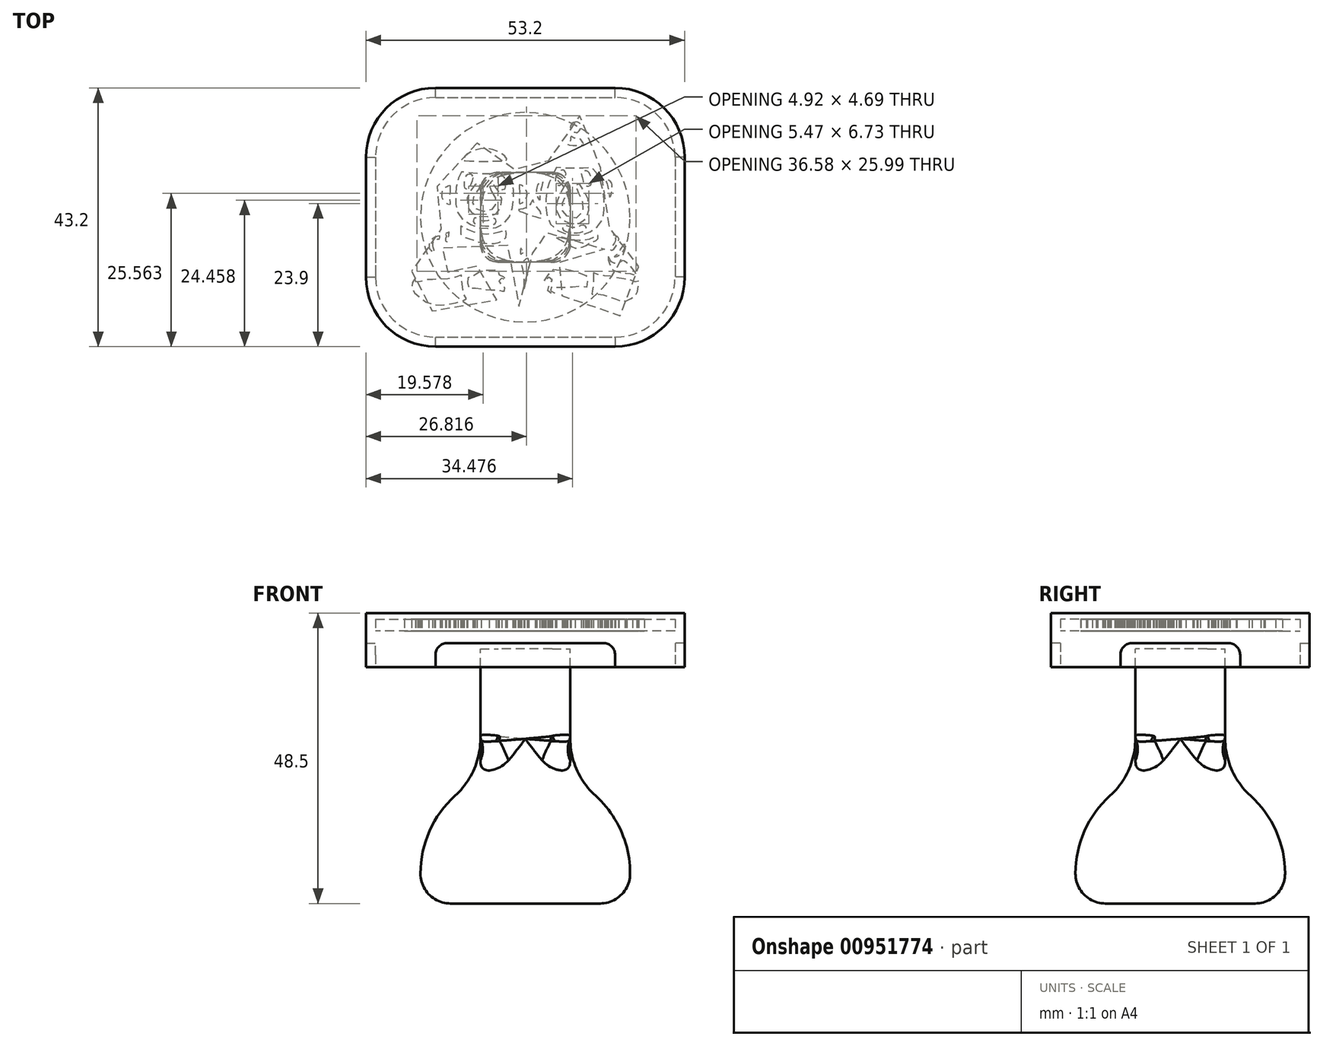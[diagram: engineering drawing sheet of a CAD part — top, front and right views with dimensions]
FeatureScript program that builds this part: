
annotation { "Feature Type Name" : "Feature", "Feature Type Description" : "" }
export const myFeature = defineFeature(function(context is Context, id is Id, definition is map)
    precondition{}
    {
        {
            var Q0;
            Q0=qCreatedBy(makeId("Top.planeOp"),FACE);
            var sketch = newSketch(context, id + "F0", { "sketchPlane" : qUnion([Q0])});
            skLineSegment(sketch, "E0.bottom", {"start": v(-25, 20) * mm, "end": v(25, 20) * mm});
            skLineSegment(sketch, "E0.top", {"start": v(-25, -20) * mm, "end": v(25, -20) * mm});
            skLineSegment(sketch, "E0.left", {"start": v(-25, 20) * mm, "end": v(-25, -20) * mm});
            skLineSegment(sketch, "E0.right", {"start": v(25, 20) * mm, "end": v(25, -20) * mm});
            skPoint(sketch, "E0.middle", {"position": v(0, 0) * mm});
            skSolve(sketch);
        }
        {
            var Q0;
            Q0 = qSketchRegion(id + "F0", true);
            extrude(context, id + "F1", {"entities" : qUnion([Q0]), "oppositeDirection" : true, "depth" : 6 * mm, "offsetDistance" : 25 * mm});
        }
        {
            var Q0;
            Q0=qCreatedBy(makeId("Top.planeOp"),FACE);
            var sketch = newSketch(context, id + "F2", { "sketchPlane" : qUnion([Q0])});
            skPoint(sketch, "E1", {"position": v(0, 16.86) * mm});
            skPoint(sketch, "E2", {"position": v(-20, 0) * mm});
            skFitSpline(sketch, "E3", {"points": [v(-8.08, 12.38) * mm, v(-8.81, 12.12) * mm, v(-9.62, 11.72) * mm, v(-10.36, 11.3) * mm, v(-10.9, 10.85) * mm, v(-11.21, 10.47) * mm, v(-11.41, 10.09) * mm, v(-11.6, 9.5) * mm, v(-11.77, 9.03) * mm, v(-11.88, 8.77) * mm, v(-11.9, 8.4) * mm, v(-11.68, 8) * mm, v(-11.76, 7.76) * mm, v(-12.03, 7.27) * mm, v(-12.19, 6.87) * mm, v(-12.34, 6.5) * mm, v(-12.45, 6.4) * mm, v(-13, 6.27) * mm, v(-13.92, 5.82) * mm, v(-14.38, 5.5) * mm, v(-14.78, 5.09) * mm, v(-15, 4.59) * mm, v(-15.05, 3.88) * mm, v(-15, 3.2) * mm, v(-14.79, 2.65) * mm, v(-14.5, 2.2) * mm, v(-13.81, 1.54) * mm, v(-13.23, 1.23) * mm, v(-12.68, 1.04) * mm, v(-12.39, 0.99) * mm, v(-12.33, 0.87) * mm, v(-12.15, 0.43) * mm, v(-11.89, -0.13) * mm, v(-11.63, -0.6) * mm, v(-11.62, -0.67) * mm, v(-11.71, -0.82) * mm, v(-12.06, -1.11) * mm, v(-12.37, -1.28) * mm, v(-12.95, -1.46) * mm, v(-13.26, -1.54) * mm, v(-13.5, -1.64) * mm, v(-14.05, -1.97) * mm, v(-14.23, -2.05) * mm, v(-14.45, -2.13) * mm, v(-14.88, -2.27) * mm, v(-15.54, -2.46) * mm, v(-16.07, -2.73) * mm, v(-16.64, -3.29) * mm, v(-16.85, -3.46) * mm, v(-17.23, -3.67) * mm, v(-17.63, -3.95) * mm, v(-17.82, -4.33) * mm, v(-17.95, -4.95) * mm, v(-17.92, -5.48) * mm, v(-17.84, -5.77) * mm, v(-17.84, -6.08) * mm, v(-17.88, -6.58) * mm, v(-17.8, -6.98) * mm, v(-17.65, -7.21) * mm, v(-17.63, -7.39) * mm, v(-17.78, -7.58) * mm, v(-18.2, -8.05) * mm, v(-18.56, -8.45) * mm, v(-18.98, -9.02) * mm, v(-19.57, -10) * mm, v(-19.88, -10.58) * mm, v(-20.17, -11.52) * mm, v(-20.16, -11.87) * mm, v(-19.7, -12.89) * mm, v(-19.23, -13.4) * mm, v(-18.28, -14.22) * mm, v(-17.78, -14.62) * mm, v(-17.3, -15.03) * mm, v(-17.25, -15.17) * mm, v(-17.34, -15.62) * mm, v(-17.34, -16.45) * mm, v(-17.23, -16.58) * mm, v(-16.53, -16.56) * mm, v(-16.4, -16.31) * mm, v(-16.3, -15.7) * mm, v(-16.24, -15.48) * mm, v(-16.1, -15.48) * mm, v(-15.79, -15.6) * mm, v(-14.78, -15.7) * mm, v(-13.86, -15.66) * mm, v(-12.92, -15.6) * mm, v(-11.74, -15.32) * mm, v(-10.78, -15.06) * mm, v(-9.64, -14.74) * mm, v(-8.83, -14.36) * mm, v(-8.48, -13.83) * mm, v(-8.4, -13.39) * mm, v(-8.38, -12.92) * mm, v(-8.3, -12.84) * mm, v(-7.52, -12.97) * mm, v(-6.65, -13.05) * mm, v(-6.12, -13.13) * mm, v(-5.83, -13.23) * mm, v(-5.71, -13.43) * mm, v(-5.36, -13.7) * mm, v(-4.81, -13.8) * mm, v(-3.92, -13.75) * mm, v(-2.96, -13.33) * mm, v(-2.56, -12.87) * mm, v(-2.31, -12.03) * mm, v(-2.15, -11.25) * mm, v(-2.12, -10.26) * mm, v(-2.34, -9.74) * mm, v(-2.6, -9.3) * mm, v(-2.9, -8.69) * mm, v(-3.33, -8.19) * mm, v(-3.98, -7.9) * mm, v(-4.6, -7.83) * mm, v(-5.42, -7.88) * mm, v(-6.2, -7.93) * mm, v(-6.94, -7.85) * mm, v(-7.5, -7.95) * mm, v(-8.18, -8.22) * mm, v(-8.73, -8.56) * mm, v(-9.1, -8.85) * mm, v(-9.27, -8.91) * mm, v(-9.53, -8.72) * mm, v(-9.98, -8.51) * mm, v(-10.56, -8.53) * mm, v(-11.24, -8.75) * mm, v(-11.61, -8.87) * mm, v(-11.5, -8.64) * mm, v(-11.36, -8.07) * mm, v(-11.23, -6.94) * mm, v(-11.3, -6.28) * mm, v(-11.6, -5.94) * mm, v(-11.9, -5.9) * mm, v(-12.14, -6.13) * mm, v(-12.26, -6.87) * mm, v(-12.35, -7.71) * mm, v(-12.59, -8.57) * mm, v(-12.82, -9.03) * mm, v(-12.96, -9.24) * mm, v(-13.83, -9.37) * mm, v(-14.94, -9.4) * mm, v(-15.96, -9.32) * mm, v(-17.1, -9.26) * mm, v(-17.68, -9.17) * mm, v(-17.64, -9.02) * mm, v(-17.3, -8.6) * mm, v(-16.63, -7.98) * mm, v(-16.22, -7.73) * mm, v(-16, -7.66) * mm, v(-15.7, -7.4) * mm, v(-15.4, -7.15) * mm, v(-15.02, -6.97) * mm, v(-14.62, -6.86) * mm, v(-14.32, -6.63) * mm, v(-14.14, -6.26) * mm, v(-14.1, -5.92) * mm, v(-14.13, -5.53) * mm, v(-14.04, -5.34) * mm, v(-13.77, -5.08) * mm, v(-13.51, -5) * mm, v(-13.1, -5.05) * mm, v(-12.67, -5.08) * mm, v(-12.36, -4.97) * mm, v(-12.08, -4.63) * mm, v(-11.97, -4.36) * mm, v(-11.85, -4.1) * mm, v(-11.51, -3.99) * mm, v(-11.16, -4.07) * mm, v(-10.2, -4.38) * mm, v(-9.16, -4.72) * mm, v(-8.27, -5.04) * mm, v(-7.47, -5.25) * mm, v(-6.7, -5.4) * mm, v(-5.86, -5.43) * mm, v(-5.09, -5.42) * mm, v(-4.26, -5.25) * mm, v(-3.4, -4.93) * mm, v(-2.8, -4.5) * mm, v(-2.38, -4.08) * mm, v(-2.2, -3.73) * mm, v(-2.1, -3.54) * mm, v(-2.04, -3.7) * mm, v(-1.94, -4.34) * mm, v(-1.89, -5.08) * mm, v(-1.8, -6.13) * mm, v(-1.75, -7.04) * mm, v(-1.64, -7.96) * mm, v(-1.55, -8.7) * mm, v(-1.37, -9.62) * mm, v(-1.28, -10.32) * mm, v(-1.26, -11.23) * mm, v(-1.18, -12.5) * mm, v(-1.14, -13.54) * mm, v(-1.07, -14.52) * mm, v(-1.03, -15.18) * mm, v(-1.03, -15.84) * mm, v(-0.99, -16.52) * mm, v(-0.91, -16.6) * mm, v(-0.24, -16.56) * mm, v(-0.15, -16.45) * mm, v(-0.12, -15.9) * mm, v(-0.1, -15.1) * mm, v(0.15, -14.32) * mm, v(0.44, -13.47) * mm, v(0.77, -12.47) * mm, v(1.03, -11.36) * mm, v(1.25, -10.24) * mm, v(1.53, -8.75) * mm, v(1.65, -7.65) * mm, v(1.62, -6.91) * mm, v(1.24, -6.04) * mm, v(0.8, -5.3) * mm, v(0.2, -4.64) * mm, v(-0.71, -3.7) * mm, v(-1.12, -3.16) * mm, v(-1.39, -2.5) * mm, v(-2.02, -1.53) * mm, v(-2.07, -1.04) * mm, v(-1.82, -0.4) * mm, v(-1.56, 0.1) * mm, v(-1.5, 0.1) * mm, v(-0.57, -0.23) * mm, v(0.59, -0.73) * mm, v(1.95, -1.15) * mm, v(3.2, -1.26) * mm, v(3.24, -1.41) * mm, v(3.5, -2.25) * mm, v(4.01, -3.47) * mm, v(4.43, -4.25) * mm, v(5.08, -4.62) * mm, v(5.89, -5) * mm, v(6.45, -5.41) * mm, v(7.16, -5.84) * mm, v(7.86, -6.1) * mm, v(8.7, -6.19) * mm, v(9.7, -5.95) * mm, v(10.43, -5.66) * mm, v(11.52, -5.18) * mm, v(12.1, -4.9) * mm, v(12.77, -4.57) * mm, v(13.43, -4.51) * mm, v(13.45, -4.59) * mm, v(13.28, -4.79) * mm, v(13.2, -5.08) * mm, v(13.19, -5.4) * mm, v(13.15, -5.47) * mm, v(12.88, -5.78) * mm, v(12.82, -6.26) * mm, v(12.84, -7.21) * mm, v(12.99, -7.78) * mm, v(13.15, -8.34) * mm, v(13.24, -8.67) * mm, v(13.19, -8.74) * mm, v(12.84, -8.7) * mm, v(11.98, -8.4) * mm, v(11.44, -8.28) * mm, v(10.58, -8.2) * mm, v(10, -8.3) * mm, v(9.5, -8.45) * mm, v(9.07, -8.34) * mm, v(8.54, -8.1) * mm, v(7.71, -7.8) * mm, v(6.76, -7.6) * mm, v(5.84, -7.56) * mm, v(5.18, -7.56) * mm, v(4.72, -7.66) * mm, v(4.3, -7.73) * mm, v(3.8, -7.71) * mm, v(3.14, -7.99) * mm, v(2.57, -8.43) * mm, v(2.17, -8.89) * mm, v(1.96, -9.36) * mm, v(1.96, -10.34) * mm, v(2.15, -11.07) * mm, v(2.51, -12.11) * mm, v(2.83, -12.72) * mm, v(3.3, -13.36) * mm, v(4.08, -13.85) * mm, v(4.67, -13.97) * mm, v(5.58, -13.87) * mm, v(5.92, -13.49) * mm, v(6.24, -12.83) * mm, v(6.51, -12.8) * mm, v(7.36, -12.72) * mm, v(7.8, -12.64) * mm, v(8.6, -12.6) * mm, v(8.95, -12.58) * mm, v(9, -12.72) * mm, v(9.18, -13.3) * mm, v(9.56, -13.66) * mm, v(10.7, -13.78) * mm, v(11.68, -13.78) * mm, v(12.4, -13.89) * mm, v(13.22, -14.1) * mm, v(14.37, -14.57) * mm, v(15.2, -14.88) * mm, v(15.66, -15.07) * mm, v(15.72, -15.37) * mm, v(15.79, -16.03) * mm, v(15.9, -16.53) * mm, v(16.17, -16.56) * mm, v(16.84, -16.56) * mm, v(16.93, -16.32) * mm, v(16.82, -15.77) * mm, v(16.82, -15.1) * mm, v(17.01, -14.99) * mm, v(17.8, -14.73) * mm, v(18.22, -14.54) * mm, v(18.73, -14.23) * mm, v(19.24, -13.9) * mm, v(19.57, -13.36) * mm, v(19.74, -12.83) * mm, v(19.85, -12.07) * mm, v(19.89, -11.15) * mm, v(19.86, -10.2) * mm, v(19.73, -9.6) * mm, v(19.46, -9.07) * mm, v(19.12, -8.51) * mm, v(18.72, -7.92) * mm, v(18.27, -7.39) * mm, v(17.93, -7.02) * mm, v(17.93, -6.9) * mm, v(18.21, -6.63) * mm, v(18.6, -5.9) * mm, v(18.63, -5.37) * mm, v(18.47, -4.95) * mm, v(18.25, -4.67) * mm, v(17.94, -4.52) * mm, v(17.69, -4.36) * mm, v(17.53, -4.12) * mm, v(17.4, -3.75) * mm, v(17.23, -3.41) * mm, v(17.02, -3.13) * mm, v(16.66, -2.94) * mm, v(16.37, -2.67) * mm, v(15.96, -2.35) * mm, v(15.55, -2.14) * mm, v(15, -2) * mm, v(14.5, -2) * mm, v(14.2, -1.9) * mm, v(13.92, -1.63) * mm, v(13.66, -1.32) * mm, v(13.67, -1.1) * mm, v(13.88, -0.65) * mm, v(13.97, -0.18) * mm, v(14.06, 0.44) * mm, v(14.15, 1.03) * mm, v(14.2, 1.38) * mm, v(14.47, 1.78) * mm, v(14.84, 2.37) * mm, v(15.37, 3.67) * mm, v(15.53, 5.33) * mm, v(15.27, 6.31) * mm, v(14.74, 6.97) * mm, v(13.91, 7.32) * mm, v(13.28, 7.49) * mm, v(12.98, 7.56) * mm, v(12.72, 8.03) * mm, v(12.44, 8.54) * mm, v(12.53, 8.85) * mm, v(12.67, 9.15) * mm, v(12.46, 9.69) * mm, v(12.2, 10.13) * mm, v(11.97, 10.53) * mm, v(11.69, 11.33) * mm, v(11.48, 11.85) * mm, v(11.22, 12.1) * mm, v(10.77, 12.24) * mm, v(10.56, 12.5) * mm, v(10.42, 13) * mm, v(10.23, 13.51) * mm, v(10.07, 13.89) * mm, v(10.16, 14.3) * mm, v(10.38, 14.8) * mm, v(10.42, 15.4) * mm, v(10.16, 16.02) * mm, v(9.86, 16.44) * mm, v(9.55, 16.73) * mm, v(9, 17) * mm, v(8.5, 17.05) * mm, v(7.99, 17.02) * mm, v(7.39, 16.74) * mm, v(7.14, 16.5) * mm, v(6.68, 15.97) * mm, v(6.46, 15.55) * mm, v(6.44, 15.09) * mm, v(6.55, 14.65) * mm, v(6.66, 14.4) * mm, v(6.66, 14.05) * mm, v(6.5, 13.45) * mm, v(6.24, 12.92) * mm, v(5.97, 12.49) * mm, v(5.78, 12.24) * mm, v(5.5, 12.15) * mm, v(5.2, 12.05) * mm, v(4.97, 11.7) * mm, v(4.67, 10.93) * mm, v(4.26, 10.25) * mm, v(3.87, 9.45) * mm, v(3.73, 9.12) * mm, v(3.8, 8.7) * mm, v(4.02, 8.38) * mm, v(3.98, 8.23) * mm, v(3.71, 7.68) * mm, v(3.44, 7.24) * mm, v(3.3, 7.04) * mm, v(2.74, 6.98) * mm, v(1.96, 6.67) * mm, v(1.46, 6.26) * mm, v(1.2, 5.76) * mm, v(1.07, 5.43) * mm, v(0.97, 5.2) * mm, v(0.87, 5.33) * mm, v(0.42, 5.91) * mm, v(-0.18, 6.26) * mm, v(-0.74, 6.28) * mm, v(-1.11, 6.44) * mm, v(-1.44, 7.12) * mm, v(-1.64, 7.55) * mm, v(-1.83, 7.88) * mm, v(-1.8, 8.15) * mm, v(-1.66, 8.68) * mm, v(-1.8, 9.16) * mm, v(-2.03, 9.65) * mm, v(-2.16, 10.31) * mm, v(-2.65, 10.97) * mm, v(-3.31, 11.5) * mm, v(-4.19, 11.93) * mm, v(-5.18, 12.3) * mm, v(-5.84, 12.41) * mm, v(-6.1, 12.82) * mm, v(-6.37, 13.35) * mm, v(-6.9, 13.8) * mm, v(-7.51, 13.95) * mm, v(-7.98, 13.77) * mm, v(-8.3, 13.5) * mm, v(-8.4, 13.02) * mm, v(-8.23, 12.63) * mm, v(-8.08, 12.38) * mm]});
            skFitSpline(sketch, "E4", {"points": [v(-14.25, -3.13) * mm, v(-14.9, -3.3) * mm, v(-15.5, -3.6) * mm, v(-15.83, -4) * mm, v(-16.03, -4.37) * mm, v(-16.1, -4.8) * mm, v(-15.98, -5.23) * mm, v(-15.74, -5.6) * mm, v(-15.38, -5.9) * mm, v(-15.2, -5.93) * mm, v(-15.17, -5.78) * mm, v(-15.25, -5.47) * mm, v(-15.37, -5.09) * mm, v(-15.44, -4.74) * mm, v(-15.44, -4.37) * mm, v(-15.32, -4.05) * mm, v(-15.15, -3.84) * mm, v(-14.8, -3.71) * mm, v(-14.45, -3.63) * mm, v(-14.28, -3.59) * mm, v(-14.25, -3.34) * mm, v(-14.25, -3.13) * mm]});
            skFitSpline(sketch, "E5", {"points": [v(-13.3, -2.78) * mm, v(-13.22, -2.97) * mm, v(-13.23, -3.26) * mm, v(-13.28, -3.52) * mm, v(-13.32, -3.68) * mm, v(-13.32, -3.87) * mm, v(-13.2, -4.02) * mm, v(-13, -4.05) * mm, v(-12.91, -3.87) * mm, v(-12.85, -3.53) * mm, v(-12.8, -3.2) * mm, v(-12.73, -2.83) * mm, v(-12.72, -2.64) * mm, v(-12.7, -2.47) * mm, v(-12.86, -2.52) * mm, v(-13.1, -2.65) * mm, v(-13.3, -2.78) * mm]});
            skFitSpline(sketch, "E6", {"points": [v(-18.37, -10.1) * mm, v(-18.57, -10.45) * mm, v(-18.79, -10.85) * mm, v(-18.93, -11.19) * mm, v(-18.98, -11.51) * mm, v(-18.98, -11.83) * mm, v(-18.83, -12.22) * mm, v(-18.42, -12.7) * mm, v(-17.77, -13.27) * mm, v(-17.1, -13.8) * mm, v(-16.76, -14.03) * mm, v(-16.24, -14.32) * mm, v(-15.5, -14.57) * mm, v(-14.67, -14.67) * mm, v(-13.93, -14.67) * mm, v(-13.3, -14.62) * mm, v(-12.61, -14.49) * mm, v(-11.77, -14.3) * mm, v(-11.28, -14.17) * mm, v(-10.61, -14) * mm, v(-10.07, -13.84) * mm, v(-9.8, -13.69) * mm, v(-9.87, -13.59) * mm, v(-10.11, -13.29) * mm, v(-10.28, -12.82) * mm, v(-10.42, -12.15) * mm, v(-10.5, -11.45) * mm, v(-10.56, -10.75) * mm, v(-10.58, -10.17) * mm, v(-10.53, -9.66) * mm, v(-10.6, -9.62) * mm, v(-10.87, -9.73) * mm, v(-11.56, -9.97) * mm, v(-12.2, -10.17) * mm, v(-13.03, -10.3) * mm, v(-13.84, -10.35) * mm, v(-14.53, -10.37) * mm, v(-15.27, -10.38) * mm, v(-16.06, -10.44) * mm, v(-16.48, -10.46) * mm, v(-16.87, -10.48) * mm, v(-17.3, -10.62) * mm, v(-17.63, -10.86) * mm, v(-17.9, -10.93) * mm, v(-18.24, -10.83) * mm, v(-18.34, -10.62) * mm, v(-18.3, -10.29) * mm, v(-18.37, -10.1) * mm]});
            skFitSpline(sketch, "E7", {"points": [v(-9.6, -10.12) * mm, v(-9.64, -10.74) * mm, v(-9.6, -11.16) * mm, v(-9.48, -11.83) * mm, v(-9.32, -11.83) * mm, v(-8.4, -11.83) * mm, v(-7.4, -11.98) * mm, v(-6.48, -12.07) * mm, v(-5.16, -12.15) * mm, v(-4.6, -12.15) * mm, v(-4.1, -12.2) * mm, v(-3.82, -12.35) * mm, v(-3.67, -12.54) * mm, v(-3.55, -12.38) * mm, v(-3.33, -12.16) * mm, v(-3.33, -11.96) * mm, v(-3.54, -11.62) * mm, v(-3.83, -11.35) * mm, v(-4.17, -11.08) * mm, v(-4.32, -10.86) * mm, v(-4.34, -10.54) * mm, v(-4.23, -10.33) * mm, v(-3.92, -10.19) * mm, v(-3.47, -10.27) * mm, v(-3.16, -10.45) * mm, v(-3.33, -10.2) * mm, v(-3.55, -10) * mm, v(-3.94, -9.82) * mm, v(-4.24, -9.68) * mm, v(-4.5, -9.44) * mm, v(-4.52, -9.16) * mm, v(-4.44, -8.96) * mm, v(-4.52, -8.83) * mm, v(-4.99, -8.82) * mm, v(-5.53, -8.87) * mm, v(-6.1, -8.93) * mm, v(-6.7, -8.94) * mm, v(-7.17, -8.9) * mm, v(-7.54, -9.1) * mm, v(-7.96, -9.35) * mm, v(-8.27, -9.6) * mm, v(-8.67, -9.84) * mm, v(-9.07, -9.98) * mm, v(-9.45, -10.03) * mm, v(-9.6, -10.12) * mm]});
            skFitSpline(sketch, "E8", {"points": [v(-10.76, -1.48) * mm, v(-10.78, -1.96) * mm, v(-10.78, -2.44) * mm, v(-10.74, -2.9) * mm, v(-10.45, -3.25) * mm, v(-9.71, -3.49) * mm, v(-8.7, -3.81) * mm, v(-8.08, -4.02) * mm, v(-7.46, -4.24) * mm, v(-6.68, -4.38) * mm, v(-6.03, -4.46) * mm, v(-5.02, -4.37) * mm, v(-4.28, -4.14) * mm, v(-3.68, -3.85) * mm, v(-3.34, -3.54) * mm, v(-3.15, -3.2) * mm, v(-3.15, -2.78) * mm, v(-3.2, -2.28) * mm, v(-3.3, -2.07) * mm, v(-3.46, -2.16) * mm, v(-4.16, -2.42) * mm, v(-4.82, -2.66) * mm, v(-5.8, -2.8) * mm, v(-7.1, -2.84) * mm, v(-8.16, -2.6) * mm, v(-9.28, -2.2) * mm, v(-9.94, -1.9) * mm, v(-10.4, -1.7) * mm, v(-10.76, -1.48) * mm]});
            skFitSpline(sketch, "E9", {"points": [v(-0.74, -5.2) * mm, v(-0.8, -5.76) * mm, v(-0.74, -6.21) * mm, v(-0.46, -5.97) * mm, v(-0.15, -5.88) * mm, v(-0.45, -5.57) * mm, v(-0.74, -5.2) * mm]});
            skFitSpline(sketch, "E10", {"points": [v(-0.17, -11.97) * mm, v(0.15, -10.7) * mm, v(0.34, -9.71) * mm, v(0.53, -8.69) * mm, v(0.6, -7.83) * mm, v(0.56, -7.08) * mm, v(0.42, -6.84) * mm, v(0.3, -6.86) * mm, v(0, -7.07) * mm, v(-0.41, -7.43) * mm, v(-0.6, -7.78) * mm, v(-0.59, -8.11) * mm, v(-0.46, -8.74) * mm, v(-0.3, -9.4) * mm, v(-0.29, -9.9) * mm, v(-0.22, -10.8) * mm, v(-0.22, -11.42) * mm, v(-0.17, -11.97) * mm]});
            skFitSpline(sketch, "E11", {"points": [v(-12.58, 5.3) * mm, v(-12.6, 3.7) * mm, v(-12.6, 2.15) * mm, v(-12.62, 2.06) * mm, v(-13.09, 2.28) * mm, v(-13.5, 2.66) * mm, v(-13.8, 3.08) * mm, v(-13.91, 3.59) * mm, v(-13.9, 4.04) * mm, v(-13.78, 4.48) * mm, v(-13.45, 4.91) * mm, v(-13.09, 5.14) * mm, v(-12.78, 5.28) * mm, v(-12.6, 5.35) * mm, v(-12.58, 5.3) * mm]});
            skFitSpline(sketch, "E12", {"points": [v(-10.65, 7.57) * mm, v(-10.95, 7.02) * mm, v(-11.32, 6.12) * mm, v(-11.58, 4.76) * mm, v(-11.64, 3.87) * mm, v(-11.64, 2.8) * mm, v(-11.48, 1.49) * mm, v(-11.2, 0.71) * mm, v(-10.6, -0.24) * mm, v(-9.56, -0.99) * mm, v(-8.31, -1.56) * mm, v(-7.08, -1.88) * mm, v(-6.11, -1.86) * mm, v(-5.02, -1.74) * mm, v(-3.97, -1.33) * mm, v(-3.2, -0.67) * mm, v(-2.53, 0.36) * mm, v(-2.13, 1.67) * mm, v(-2, 2.82) * mm, v(-1.95, 4.1) * mm, v(-2, 5.14) * mm, v(-2.25, 6.3) * mm, v(-2.49, 6.9) * mm, v(-2.78, 7.4) * mm, v(-3.1, 7.43) * mm, v(-3.75, 7.33) * mm, v(-4.75, 7.27) * mm, v(-6.21, 7.21) * mm, v(-7.74, 7.25) * mm, v(-9.28, 7.41) * mm, v(-10, 7.5) * mm, v(-10.65, 7.57) * mm]});
            skFitSpline(sketch, "E13", {"points": [v(-10.04, 9.43) * mm, v(-8.7, 9.37) * mm, v(-6.45, 9.35) * mm, v(-4.55, 9.37) * mm, v(-3.44, 9.41) * mm, v(-3.06, 9.55) * mm, v(-3.1, 9.83) * mm, v(-3.54, 10.34) * mm, v(-4.7, 11.04) * mm, v(-5.76, 11.34) * mm, v(-6.68, 11.47) * mm, v(-7.8, 11.38) * mm, v(-8.99, 10.96) * mm, v(-9.84, 10.4) * mm, v(-10.37, 9.8) * mm, v(-10.5, 9.51) * mm, v(-10.3, 9.43) * mm, v(-10.04, 9.43) * mm]});
            skFitSpline(sketch, "E14", {"points": [v(-8.16, -0.14) * mm, v(-8.47, -0.12) * mm, v(-8.6, -0.28) * mm, v(-8.7, -0.51) * mm, v(-8.64, -0.86) * mm, v(-8.35, -1.1) * mm, v(-7.9, -1.27) * mm, v(-7.39, -1.4) * mm, v(-6.68, -1.46) * mm, v(-6.07, -1.45) * mm, v(-5.57, -1.3) * mm, v(-5.14, -1.1) * mm, v(-4.94, -0.92) * mm, v(-4.88, -0.57) * mm, v(-4.97, -0.3) * mm, v(-5.23, -0.22) * mm, v(-5.57, -0.3) * mm, v(-5.88, -0.46) * mm, v(-6.25, -0.57) * mm, v(-6.68, -0.62) * mm, v(-7.11, -0.61) * mm, v(-7.55, -0.49) * mm, v(-7.87, -0.31) * mm, v(-8.16, -0.14) * mm]});
            skFitSpline(sketch, "E15", {"points": [v(-5.63, 4.33) * mm, v(-5.4, 3.94) * mm, v(-5.06, 3.3) * mm, v(-4.9, 2.82) * mm, v(-4.93, 2.3) * mm, v(-5.1, 1.84) * mm, v(-5.35, 1.52) * mm, v(-5.64, 1.27) * mm, v(-6.27, 1.02) * mm, v(-7, 0.94) * mm, v(-7.74, 1.13) * mm, v(-8.13, 1.34) * mm, v(-8.47, 1.75) * mm, v(-8.74, 2.22) * mm, v(-8.74, 2.82) * mm, v(-8.64, 3.42) * mm, v(-8.36, 3.96) * mm, v(-7.93, 4.5) * mm, v(-7.58, 4.82) * mm, v(-7.37, 5.18) * mm, v(-7.46, 5.57) * mm, v(-7.7, 5.72) * mm, v(-8.04, 5.7) * mm, v(-8.54, 5.3) * mm, v(-8.9, 4.84) * mm, v(-9.27, 4.28) * mm, v(-9.53, 3.71) * mm, v(-9.72, 2.92) * mm, v(-9.73, 2.15) * mm, v(-9.62, 1.6) * mm, v(-9.35, 1.1) * mm, v(-8.95, 0.75) * mm, v(-8.36, 0.39) * mm, v(-7.58, 0.17) * mm, v(-6.81, 0.1) * mm, v(-5.93, 0.17) * mm, v(-5.07, 0.46) * mm, v(-4.7, 0.71) * mm, v(-4.36, 1.15) * mm, v(-4, 1.93) * mm, v(-3.93, 2.7) * mm, v(-4.05, 3.53) * mm, v(-4.32, 4.09) * mm, v(-4.75, 4.77) * mm, v(-5.07, 5.14) * mm, v(-5.36, 5.46) * mm, v(-5.67, 5.48) * mm, v(-5.94, 5.37) * mm, v(-6.03, 5.02) * mm, v(-5.9, 4.62) * mm, v(-5.63, 4.33) * mm]});
            skFitSpline(sketch, "E16", {"points": [v(-4.48, 6.66) * mm, v(-4.57, 6.5) * mm, v(-4.57, 6.17) * mm, v(-4.53, 5.7) * mm, v(-4.46, 5.16) * mm, v(-4.22, 4.77) * mm, v(-3.92, 4.63) * mm, v(-3.52, 4.7) * mm, v(-3.35, 4.9) * mm, v(-3.3, 5.5) * mm, v(-3.31, 6.13) * mm, v(-3.44, 6.59) * mm, v(-3.76, 6.85) * mm, v(-4.23, 6.84) * mm, v(-4.48, 6.66) * mm]});
            skFitSpline(sketch, "E17", {"points": [v(-8.77, 6.85) * mm, v(-8.85, 7) * mm, v(-9.1, 7.14) * mm, v(-9.47, 7.14) * mm, v(-9.83, 7) * mm, v(-10, 6.64) * mm, v(-10.15, 6.2) * mm, v(-10.23, 5.74) * mm, v(-10.25, 5.4) * mm, v(-10.2, 5.01) * mm, v(-10.08, 4.86) * mm, v(-9.88, 4.76) * mm, v(-9.63, 4.76) * mm, v(-9.38, 4.92) * mm, v(-9.14, 5.26) * mm, v(-8.93, 5.77) * mm, v(-8.8, 6.22) * mm, v(-8.72, 6.59) * mm, v(-8.77, 6.85) * mm]});
            skFitSpline(sketch, "E18", {"points": [v(3.17, -10.64) * mm, v(3.32, -10.25) * mm, v(3.6, -9.92) * mm, v(3.95, -9.6) * mm, v(4.23, -9.22) * mm, v(4.23, -8.9) * mm, v(4.23, -8.71) * mm, v(4.46, -8.67) * mm, v(5.08, -8.76) * mm, v(5.45, -8.83) * mm, v(5.86, -8.86) * mm, v(6.14, -8.76) * mm, v(6.24, -8.57) * mm, v(6.51, -8.58) * mm, v(7.04, -8.71) * mm, v(8.15, -9.02) * mm, v(9.01, -9.3) * mm, v(9.83, -9.63) * mm, v(10.22, -9.78) * mm, v(10.38, -9.9) * mm, v(10.41, -10.23) * mm, v(10.4, -11.06) * mm, v(10.28, -11.67) * mm, v(10.17, -11.68) * mm, v(9.71, -11.57) * mm, v(9.14, -11.57) * mm, v(8.13, -11.64) * mm, v(7.43, -11.73) * mm, v(6.7, -11.78) * mm, v(5.88, -11.81) * mm, v(5.34, -11.75) * mm, v(4.92, -11.65) * mm, v(4.46, -11.59) * mm, v(4.18, -11.72) * mm, v(4.12, -12.03) * mm, v(4.25, -12.32) * mm, v(4.47, -12.48) * mm, v(4.83, -12.63) * mm, v(5.08, -12.74) * mm, v(5.01, -12.9) * mm, v(4.72, -12.92) * mm, v(4.25, -12.74) * mm, v(3.86, -12.42) * mm, v(3.74, -12.01) * mm, v(3.84, -11.62) * mm, v(4.1, -11.16) * mm, v(4.34, -10.84) * mm, v(4.5, -10.44) * mm, v(4.4, -10.15) * mm, v(4.17, -10) * mm, v(3.87, -10.05) * mm, v(3.6, -10.23) * mm, v(3.17, -10.64) * mm]});
            skFitSpline(sketch, "E19", {"points": [v(11.4, -9.3) * mm, v(11.36, -10) * mm, v(11.36, -11.02) * mm, v(11.31, -11.93) * mm, v(11.18, -12.4) * mm, v(11, -12.73) * mm, v(11.05, -12.83) * mm, v(11.59, -12.83) * mm, v(12.47, -12.83) * mm, v(13.1, -13) * mm, v(14, -13.3) * mm, v(14.95, -13.6) * mm, v(15.68, -13.9) * mm, v(16.1, -14.03) * mm, v(16.76, -14) * mm, v(17.28, -13.77) * mm, v(17.8, -13.51) * mm, v(18.32, -13.22) * mm, v(18.65, -12.7) * mm, v(18.78, -12.14) * mm, v(18.91, -11.34) * mm, v(18.93, -10.82) * mm, v(18.91, -10.62) * mm, v(18.72, -10.7) * mm, v(18.36, -10.79) * mm, v(17.77, -10.6) * mm, v(17.05, -10.38) * mm, v(15.78, -10.23) * mm, v(14.8, -9.99) * mm, v(14.07, -9.8) * mm, v(13.33, -9.78) * mm, v(12.57, -9.66) * mm, v(11.64, -9.44) * mm, v(11.4, -9.3) * mm]});
            skFitSpline(sketch, "E20", {"points": [v(13.87, -6.55) * mm, v(13.87, -7) * mm, v(14, -7.6) * mm, v(14.35, -8.4) * mm, v(14.69, -8.86) * mm, v(15.1, -9) * mm, v(16.07, -9.24) * mm, v(17.2, -9.36) * mm, v(17.94, -9.54) * mm, v(18.3, -9.67) * mm, v(18.6, -9.84) * mm, v(18.6, -9.7) * mm, v(18.33, -9.16) * mm, v(17.93, -8.6) * mm, v(17.44, -8.03) * mm, v(16.99, -7.68) * mm, v(16.6, -7.34) * mm, v(16.4, -7.19) * mm, v(16.22, -7.27) * mm, v(15.85, -7.49) * mm, v(15.5, -7.64) * mm, v(15.2, -7.7) * mm, v(14.68, -7.65) * mm, v(14.3, -7.38) * mm, v(14.1, -7) * mm, v(13.87, -6.55) * mm]});
            skFitSpline(sketch, "E21", {"points": [v(16.54, -4.4) * mm, v(16.62, -4.86) * mm, v(16.51, -5.26) * mm, v(16.1, -5.96) * mm, v(15.73, -6.34) * mm, v(15.34, -6.6) * mm, v(14.96, -6.69) * mm, v(14.96, -6.48) * mm, v(15.17, -6.3) * mm, v(15.73, -5.8) * mm, v(15.9, -5.43) * mm, v(16.16, -4.98) * mm, v(16.39, -4.59) * mm, v(16.54, -4.4) * mm]});
            skFitSpline(sketch, "E22", {"points": [v(14.26, -5.39) * mm, v(14.33, -5.55) * mm, v(14.57, -5.44) * mm, v(15.14, -4.87) * mm, v(15.5, -4.14) * mm, v(15.6, -3.61) * mm, v(15.42, -3.32) * mm, v(14.94, -3.05) * mm, v(14.47, -3.04) * mm, v(14.7, -3.16) * mm, v(15, -3.39) * mm, v(15.08, -3.7) * mm, v(14.97, -4.11) * mm, v(14.72, -4.56) * mm, v(14.48, -4.95) * mm, v(14.26, -5.39) * mm]});
            skFitSpline(sketch, "E23", {"points": [v(5.2, -3.34) * mm, v(6.33, -4.05) * mm, v(7.5, -4.75) * mm, v(8.18, -5.09) * mm, v(9.01, -5.14) * mm, v(9.95, -4.78) * mm, v(10.52, -4.46) * mm, v(11.38, -4.05) * mm, v(12.09, -3.7) * mm, v(12.14, -3.26) * mm, v(12.11, -2.93) * mm, v(11.83, -3.08) * mm, v(10.68, -3.7) * mm, v(8.98, -3.87) * mm, v(7.96, -3.83) * mm, v(6.83, -3.7) * mm, v(5.2, -3.34) * mm]});
            skFitSpline(sketch, "E24", {"points": [v(-0.99, 5.38) * mm, v(-0.93, 4.2) * mm, v(-1.03, 2.34) * mm, v(-0.93, 2.26) * mm, v(-0.35, 2.52) * mm, v(0.26, 3.44) * mm, v(0.18, 4.4) * mm, v(-0.35, 5.16) * mm, v(-0.78, 5.36) * mm, v(-0.99, 5.38) * mm]});
            skFitSpline(sketch, "E25", {"points": [v(2.9, 5.87) * mm, v(2.8, 5.4) * mm, v(2.57, 4.32) * mm, v(2.4, 3.07) * mm, v(2.43, 2.82) * mm, v(2.14, 3.34) * mm, v(1.96, 4.1) * mm, v(1.96, 4.83) * mm, v(2.16, 5.45) * mm, v(2.61, 5.85) * mm, v(2.9, 5.87) * mm]});
            skFitSpline(sketch, "E26", {"points": [v(13.49, 6.12) * mm, v(13.65, 5.5) * mm, v(13.88, 4.67) * mm, v(14.02, 3.81) * mm, v(14.06, 3.34) * mm, v(14.24, 3.59) * mm, v(14.49, 4.95) * mm, v(14.37, 5.8) * mm, v(13.86, 6.2) * mm, v(13.45, 6.37) * mm, v(13.49, 6.12) * mm]});
            skFitSpline(sketch, "E27", {"points": [v(8.26, 15.9) * mm, v(7.68, 15.53) * mm, v(7.55, 14.84) * mm, v(7.9, 14.4) * mm, v(8.56, 14.13) * mm, v(9.01, 14.43) * mm, v(9.36, 15.12) * mm, v(9.01, 15.73) * mm, v(8.26, 15.9) * mm]});
            skFitSpline(sketch, "E28", {"points": [v(7.08, 12.17) * mm, v(9.68, 12.13) * mm, v(9.58, 12.5) * mm, v(9.19, 13.03) * mm, v(8.6, 13.16) * mm, v(8.13, 13.25) * mm, v(7.66, 13.46) * mm, v(7.57, 13.18) * mm, v(7.36, 12.5) * mm, v(7.08, 12.17) * mm]});
            skFitSpline(sketch, "E29", {"points": [v(-0.99, 1.04) * mm, v(0.77, 0.4) * mm, v(1.95, 0) * mm, v(2.74, -0.16) * mm, v(2.64, 0.21) * mm, v(2.54, 0.92) * mm, v(2.22, 1.37) * mm, v(1.7, 1.97) * mm, v(1.38, 2.62) * mm, v(1.24, 2.93) * mm, v(1.08, 2.71) * mm, v(0.86, 2.18) * mm, v(0.45, 1.8) * mm, v(-0.18, 1.47) * mm, v(-0.77, 1.36) * mm, v(-1.16, 1.22) * mm, v(-0.99, 1.04) * mm]});
            skFitSpline(sketch, "E30", {"points": [v(5.2, 8.3) * mm, v(4.56, 7) * mm, v(3.91, 5.57) * mm, v(3.5, 3.92) * mm, v(3.44, 2.38) * mm, v(3.54, 0.65) * mm, v(4.09, -0.95) * mm, v(5.58, -2.3) * mm, v(6.9, -2.83) * mm, v(8.57, -2.99) * mm, v(10.31, -2.68) * mm, v(11.6, -1.93) * mm, v(12.8, -0.62) * mm, v(13.2, 1.67) * mm, v(13.05, 3.82) * mm, v(12.6, 5.88) * mm, v(11.78, 7.58) * mm, v(11.21, 8.23) * mm, v(10.92, 8.23) * mm, v(5.54, 8.29) * mm, v(5.2, 8.3) * mm]});
            skFitSpline(sketch, "E31", {"points": [v(5.52, 7.4) * mm, v(5.1, 6.64) * mm, v(5.03, 5.96) * mm, v(5.16, 5.53) * mm, v(5.52, 5.35) * mm, v(5.89, 5.41) * mm, v(6.38, 6.06) * mm, v(6.67, 6.74) * mm, v(6.8, 7.29) * mm, v(6.57, 7.7) * mm, v(6.2, 7.88) * mm, v(5.77, 7.72) * mm, v(5.52, 7.4) * mm]});
            skFitSpline(sketch, "E32", {"points": [v(9.37, 7.29) * mm, v(9.55, 6.6) * mm, v(9.65, 6) * mm, v(9.78, 5.55) * mm, v(10.12, 5.23) * mm, v(10.57, 5.2) * mm, v(10.96, 5.43) * mm, v(11.06, 5.92) * mm, v(10.94, 6.68) * mm, v(10.78, 7.25) * mm, v(10.45, 7.64) * mm, v(10.04, 7.76) * mm, v(9.57, 7.6) * mm, v(9.37, 7.29) * mm]});
            skFitSpline(sketch, "E33", {"points": [v(6.79, -1.32) * mm, v(7.55, -1.6) * mm, v(8.34, -1.66) * mm, v(8.94, -1.5) * mm, v(9.43, -1.3) * mm, v(9.82, -1.34) * mm, v(10.12, -1.64) * mm, v(10.08, -2.05) * mm, v(9.69, -2.36) * mm, v(9.08, -2.6) * mm, v(8.5, -2.66) * mm, v(7.87, -2.66) * mm, v(6.95, -2.48) * mm, v(6.42, -2.17) * mm, v(6.3, -1.76) * mm, v(6.48, -1.4) * mm, v(6.79, -1.32) * mm]});
            skFitSpline(sketch, "E34", {"points": [v(6.67, 5.43) * mm, v(6.18, 4.63) * mm, v(5.67, 3.73) * mm, v(5.38, 2.88) * mm, v(5.18, 1.9) * mm, v(5.2, 0.95) * mm, v(5.83, -0.2) * mm, v(6.46, -0.66) * mm, v(7.7, -1.07) * mm, v(8.85, -1.03) * mm, v(9.63, -0.78) * mm, v(10.25, 0) * mm, v(10.55, 0.77) * mm, v(10.65, 1.79) * mm, v(10.41, 3.28) * mm, v(10.04, 4.02) * mm, v(9.57, 4.86) * mm, v(9.14, 5.49) * mm, v(8.85, 5.66) * mm, v(8.53, 5.6) * mm, v(8.34, 5.3) * mm, v(8.61, 4.5) * mm, v(9.14, 3.55) * mm, v(9.55, 2.6) * mm, v(9.69, 1.57) * mm, v(9.41, 0.4) * mm, v(8.5, -0.14) * mm, v(7.27, 0) * mm, v(6.74, 0.41) * mm, v(6.39, 0.8) * mm, v(6.19, 1.4) * mm, v(6.15, 2.13) * mm, v(6.37, 2.85) * mm, v(6.93, 3.9) * mm, v(7.3, 4.54) * mm, v(7.57, 5.1) * mm, v(7.63, 5.56) * mm, v(7.43, 5.82) * mm, v(7.01, 5.83) * mm, v(6.77, 5.63) * mm, v(6.67, 5.43) * mm]});
            skSolve(sketch);
        }
        {
            var Q0;
            Q0 = qSketchRegion(id + "F2", true);
            var Q1;
            Q1=makeQuery(id+"F2.imprint","IMPRINT",FACE,{"disambiguationData":[TD([[makeQuery(id+"F2.imprint","IMPRINT",EDGE,{"derivedFrom":sQuery(id+"F2.wireOp",EDGE,"E17")}),1.0]])]});
            var Q2;
            Q2=makeQuery(id+"F2.imprint","IMPRINT",FACE,{"disambiguationData":[TD([[makeQuery(id+"F2.imprint","IMPRINT",EDGE,{"derivedFrom":sQuery(id+"F2.wireOp",EDGE,"E15")}),1.0]])]});
            var Q3;
            Q3=makeQuery(id+"F2.imprint","IMPRINT",FACE,{"disambiguationData":[TD([[makeQuery(id+"F2.imprint","IMPRINT",EDGE,{"derivedFrom":sQuery(id+"F2.wireOp",EDGE,"E16")}),1.0]])]});
            var Q4;
            Q4=makeQuery(id+"F2.imprint","IMPRINT",FACE,{"disambiguationData":[TD([[makeQuery(id+"F2.imprint","IMPRINT",EDGE,{"derivedFrom":sQuery(id+"F2.wireOp",EDGE,"E14")}),1.0]])]});
            var Q5;
            Q5=makeQuery(id+"F2.imprint","IMPRINT",FACE,{"disambiguationData":[TD([[makeQuery(id+"F2.imprint","IMPRINT",EDGE,{"derivedFrom":sQuery(id+"F2.wireOp",EDGE,"E31")}),1.0]])]});
            var Q6;
            Q6=makeQuery(id+"F2.imprint","IMPRINT",FACE,{"disambiguationData":[TD([[makeQuery(id+"F2.imprint","IMPRINT",EDGE,{"derivedFrom":sQuery(id+"F2.wireOp",EDGE,"E32")}),1.0]])]});
            var Q7;
            Q7=makeQuery(id+"F2.imprint","IMPRINT",FACE,{"disambiguationData":[TD([[makeQuery(id+"F2.imprint","IMPRINT",EDGE,{"derivedFrom":sQuery(id+"F2.wireOp",EDGE,"E34")}),1.0]])]});
            var Q8;
            Q8=makeQuery(id+"F2.imprint","IMPRINT",FACE,{"disambiguationData":[TD([[makeQuery(id+"F2.imprint","IMPRINT",EDGE,{"derivedFrom":sQuery(id+"F2.wireOp",EDGE,"E33")}),-1.0]])]});
            extrude(context, id + "F3", {"entities" : qUnion([Q0, Q1, Q2, Q3, Q4, Q5, Q6, Q7, Q8]), "operationType" : NewBodyOperationType.ADD, "depth" : 2 * mm, "offsetDistance" : 25 * mm});
        }
        {
            var Q0;
            Q0=makeQuery(id+"F1.opExtrude","CAP_FACE",FACE,{"disambiguationData":[OSD([sQuery(id+"F0.wireOp",EDGE,"E0.bottom"),sQuery(id+"F0.wireOp",EDGE,"E0.top"),sQuery(id+"F0.wireOp",EDGE,"E0.left"),sQuery(id+"F0.wireOp",EDGE,"E0.right")])],"isStart":false});
            var sketch = newSketch(context, id + "F4", { "sketchPlane" : qUnion([Q0])});
            skLineSegment(sketch, "E35.bottom", {"start": v(4.5, -7.5) * mm, "end": v(-4.5, -7.5) * mm});
            skLineSegment(sketch, "E35.top", {"start": v(4.5, 7.5) * mm, "end": v(-4.5, 7.5) * mm});
            skLineSegment(sketch, "E35.left", {"start": v(7.5, -4.5) * mm, "end": v(7.5, 4.5) * mm});
            skLineSegment(sketch, "E35.right", {"start": v(-7.5, -4.5) * mm, "end": v(-7.5, 4.5) * mm});
            skPoint(sketch, "E35.middle", {"position": v(0, 0) * mm});
            skPoint(sketch, "E36.visualSharp", {"position": v(7.5, -7.5) * mm});
            skArc(sketch, "E36.filletArc", {"start": v(4.5, -7.5) * mm, "mid": v(6.62, -6.62) * mm, "end": v(7.5, -4.5) * mm});
            skPoint(sketch, "E37.visualSharp", {"position": v(-7.5, -7.5) * mm});
            skArc(sketch, "E37.filletArc", {"start": v(-7.5, -4.5) * mm, "mid": v(-6.62, -6.62) * mm, "end": v(-4.5, -7.5) * mm});
            skPoint(sketch, "E38.visualSharp", {"position": v(-7.5, 7.5) * mm});
            skArc(sketch, "E38.filletArc", {"start": v(-4.5, 7.5) * mm, "mid": v(-6.62, 6.62) * mm, "end": v(-7.5, 4.5) * mm});
            skPoint(sketch, "E39.visualSharp", {"position": v(7.5, 7.5) * mm});
            skArc(sketch, "E39.filletArc", {"start": v(7.5, 4.5) * mm, "mid": v(6.62, 6.62) * mm, "end": v(4.5, 7.5) * mm});
            skSolve(sketch);
        }
        {
            var Q0;
            Q0 = qSketchRegion(id + "F4", true);
            extrude(context, id + "F5", {"entities" : qUnion([Q0]), "operationType" : NewBodyOperationType.REMOVE, "oppositeDirection" : true, "depth" : 3 * mm, "offsetDistance" : 25 * mm});
        }
        {
            var Q0;
            Q0=makeQuery(id+"F5.boolean.opBoolean","COPY",FACE,{"derivedFrom":makeQuery(id+"F5.opExtrude","CAP_FACE",FACE,{"disambiguationData":[OSD([sQuery(id+"F4.wireOp",EDGE,"E35.bottom"),sQuery(id+"F4.wireOp",EDGE,"E35.top"),sQuery(id+"F4.wireOp",EDGE,"E35.left"),sQuery(id+"F4.wireOp",EDGE,"E35.right")])],"isStart":false})});
            var sketch = newSketch(context, id + "F6", { "sketchPlane" : qUnion([Q0])});
            skLineSegment(sketch, "E40.0", {"start": v(4.5, -7.5) * mm, "end": v(-4.5, -7.5) * mm});
            skArc(sketch, "E40.1", {"start": v(4.5, -7.5) * mm, "mid": v(6.62, -6.62) * mm, "end": v(7.5, -4.5) * mm});
            skLineSegment(sketch, "E40.2", {"start": v(7.5, -4.5) * mm, "end": v(7.5, 4.5) * mm});
            skArc(sketch, "E40.3", {"start": v(7.5, 4.5) * mm, "mid": v(6.62, 6.62) * mm, "end": v(4.5, 7.5) * mm});
            skLineSegment(sketch, "E40.4", {"start": v(4.5, 7.5) * mm, "end": v(-4.5, 7.5) * mm});
            skArc(sketch, "E40.5", {"start": v(-4.5, 7.5) * mm, "mid": v(-6.62, 6.62) * mm, "end": v(-7.5, 4.5) * mm});
            skLineSegment(sketch, "E40.6", {"start": v(-7.5, -4.5) * mm, "end": v(-7.5, 4.5) * mm});
            skArc(sketch, "E40.7", {"start": v(-7.5, -4.5) * mm, "mid": v(-6.62, -6.62) * mm, "end": v(-4.5, -7.5) * mm});
            skSolve(sketch);
        }
        {
            var Q0;
            Q0 = qSketchRegion(id + "F6", true);
            var Q1;
            Q1=makeQuery(id+"F1.opExtrude","CAP_FACE",FACE,{"disambiguationData":[OSD([sQuery(id+"F0.wireOp",EDGE,"E0.bottom"),sQuery(id+"F0.wireOp",EDGE,"E0.top"),sQuery(id+"F0.wireOp",EDGE,"E0.left"),sQuery(id+"F0.wireOp",EDGE,"E0.right")])],"isStart":false});
            extrude(context, id + "F7", {"entities" : qUnion([Q0]), "depth" : 15 * mm, "endBoundEntityFace" : qUnion([Q1]), "offsetDistance" : 25 * mm});
        }
        {
            var Q0;
            Q0=makeQuery(id+"F1.opExtrude","SWEPT_EDGE",EDGE,{"disambiguationData":[OSD([sQuery(id+"F0.wireOp",EDGE,"E0.top"),sQuery(id+"F0.wireOp",EDGE,"E0.left")])]});
            var Q1;
            Q1=makeQuery(id+"F1.opExtrude","SWEPT_EDGE",EDGE,{"disambiguationData":[OSD([sQuery(id+"F0.wireOp",EDGE,"E0.top"),sQuery(id+"F0.wireOp",EDGE,"E0.right")])]});
            var Q2;
            Q2=makeQuery(id+"F1.opExtrude","SWEPT_EDGE",EDGE,{"disambiguationData":[OSD([sQuery(id+"F0.wireOp",EDGE,"E0.bottom"),sQuery(id+"F0.wireOp",EDGE,"E0.left")])]});
            var Q3;
            Q3=makeQuery(id+"F1.opExtrude","SWEPT_EDGE",EDGE,{"disambiguationData":[OSD([sQuery(id+"F0.wireOp",EDGE,"E0.bottom"),sQuery(id+"F0.wireOp",EDGE,"E0.right")])]});
            fillet(context, id + "F8", {"entities" : qUnion([Q0, Q1, Q2, Q3]), "radius" : 10 * mm, "tangentPropagation" : true, "allowEdgeOverflow" : false});
        }
        {
            var Q0;
            Q0=qCreatedBy(makeId("Front.planeOp"),FACE);
            var sketch = newSketch(context, id + "F9", { "sketchPlane" : qUnion([Q0])});
            skCircle(sketch, "E41", {"center": v(0, -40.5) * mm, "radius": 17.5 * mm});
            skPoint(sketch, "E42.0", {"position": v(-7.5, -18) * mm});
            skArc(sketch, "E43", {"start": v(-11.73, -27.51) * mm, "mid": v(-8.6, -23.2) * mm, "end": v(-7.5, -18) * mm});
            skLineSegment(sketch, "E44", {"start": v(-7.5, -18) * mm, "end": v(0, -18) * mm});
            skLineSegment(sketch, "E45", {"start": v(0, -18) * mm, "end": v(0, -58) * mm});
            skCircle(sketch, "E46", {"center": v(-12.5, -40.5) * mm, "radius": 5 * mm});
            skLineSegment(sketch, "E47", {"start": v(-12.5, -45.5) * mm, "end": v(0, -45.5) * mm});
            skSolve(sketch);
        }
        {
            var Q0;
            {var subQ0=sQuery(id+"F9.wireOp",EDGE,"E41");var subQ1=makeQuery(id+"F9.imprint","INTERSECT",VERTEX,{"derivedFrom":[subQ0,sQuery(id+"F9.wireOp",EDGE,"E43")]});Q0=makeQuery(id+"F9.imprint","IMPRINT",FACE,{"disambiguationData":[TD([[makeQuery(id+"F9.imprint","IMPRINT",EDGE,{"disambiguationData":[TD([[subQ1,1.0]])],"derivedFrom":subQ0}),1.0]])]});}
            var Q1;
            {var subQ0=sQuery(id+"F9.wireOp",EDGE,"E43");Q1=makeQuery(id+"F9.imprint","IMPRINT",FACE,{"disambiguationData":[TD([[makeQuery(id+"F9.imprint","IMPRINT",EDGE,{"derivedFrom":subQ0}),-1.0]])]});}
            var Q2;
            {var subQ0=sQuery(id+"F9.wireOp",EDGE,"E46");var subQ1=makeQuery(id+"F9.imprint","INTERSECT",VERTEX,{"derivedFrom":[subQ0,sQuery(id+"F9.wireOp",EDGE,"E47")]});Q2=makeQuery(id+"F9.imprint","IMPRINT",FACE,{"disambiguationData":[TD([[makeQuery(id+"F9.imprint","IMPRINT",EDGE,{"disambiguationData":[TD([[subQ1,1.0]])],"derivedFrom":subQ0}),1.0]])]});}
            var Q3;
            Q3=sQuery(id+"F9.wireOp",EDGE,"E45");
            revolve(context, id + "F10", {"operationType" : NewBodyOperationType.ADD, "surfaceOperationType" : NewSurfaceOperationType.NEW, "entities" : qUnion([Q0, Q1, Q2]), "axis" : qUnion([Q3]), "revolveType" : RevolveType.FULL});
        }
        {
            var Q0;
            {var subQ0=sQuery(id+"F6.wireOp",EDGE,"E40.0");var subQ1=sQuery(id+"F9.wireOp",EDGE,"E43");var subQ2=sQuery(id+"F6.wireOp",EDGE,"E40.2");Q0=makeQuery(id+"F10.boolean.opBoolean","SPLIT",EDGE,{"disambiguationData":[TD([makeQuery(id+"F7.opExtrude","SWEPT_FACE",FACE,{"disambiguationData":[OSD([subQ0])]}),makeQuery(id+"F7.opExtrude","CAP_FACE",FACE,{"disambiguationData":[OSD([subQ0,sQuery(id+"F6.wireOp",EDGE,"E40.1"),subQ2,sQuery(id+"F6.wireOp",EDGE,"E40.3"),sQuery(id+"F6.wireOp",EDGE,"E40.4"),sQuery(id+"F6.wireOp",EDGE,"E40.5"),sQuery(id+"F6.wireOp",EDGE,"E40.6"),sQuery(id+"F6.wireOp",EDGE,"E40.7")])],"isStart":false}),makeQuery(id+"F7.opExtrude","SWEPT_FACE",FACE,{"disambiguationData":[OSD([subQ2])]}),makeQuery(id+"F10.opRevolve","SWEPT_FACE",FACE,{"disambiguationData":[OSD([subQ1])]})])],"derivedFrom":makeQuery(id+"F10.opRevolve","SWEPT_EDGE",EDGE,{"disambiguationData":[OSD([subQ1,sQuery(id+"F9.wireOp",EDGE,"E44")])]})});}
            fillet(context, id + "F11", {"entities" : qUnion([Q0]), "radius" : 5 * mm, "tangentPropagation" : true, "allowEdgeOverflow" : false});
        }
        {
            var Q0;
            {var subQ0=sQuery(id+"F6.wireOp",EDGE,"E40.7");var subQ1=sQuery(id+"F6.wireOp",EDGE,"E40.0");var subQ2=sQuery(id+"F9.wireOp",EDGE,"E43");var subQ3=sQuery(id+"F6.wireOp",EDGE,"E40.6");Q0=makeQuery(id+"F11.opFillet","BLEND_EDGE",EDGE,{"blendedFrom":[makeQuery(id+"F10.boolean.opBoolean","SPLIT",EDGE,{"disambiguationData":[TD([makeQuery(id+"F7.opExtrude","SWEPT_FACE",FACE,{"disambiguationData":[OSD([subQ1])]}),makeQuery(id+"F7.opExtrude","CAP_FACE",FACE,{"disambiguationData":[OSD([subQ1,sQuery(id+"F6.wireOp",EDGE,"E40.1"),sQuery(id+"F6.wireOp",EDGE,"E40.2"),sQuery(id+"F6.wireOp",EDGE,"E40.3"),sQuery(id+"F6.wireOp",EDGE,"E40.4"),sQuery(id+"F6.wireOp",EDGE,"E40.5"),subQ3,subQ0])],"isStart":false}),makeQuery(id+"F7.opExtrude","SWEPT_FACE",FACE,{"disambiguationData":[OSD([subQ3])]}),makeQuery(id+"F10.opRevolve","SWEPT_FACE",FACE,{"disambiguationData":[OSD([subQ2])]})])],"derivedFrom":makeQuery(id+"F10.opRevolve","SWEPT_EDGE",EDGE,{"disambiguationData":[OSD([subQ2,sQuery(id+"F9.wireOp",EDGE,"E44")])]})}),makeQuery(id+"F7.opExtrude","SWEPT_FACE",FACE,{"disambiguationData":[OSD([subQ0])]})],"blendedInto":[makeQuery(id+"F7.opExtrude","SWEPT_FACE",FACE,{"disambiguationData":[OSD([subQ0])]})]});}
            var Q1;
            {var subQ0=sQuery(id+"F6.wireOp",EDGE,"E40.1");var subQ1=sQuery(id+"F6.wireOp",EDGE,"E40.0");var subQ2=sQuery(id+"F9.wireOp",EDGE,"E43");var subQ3=sQuery(id+"F6.wireOp",EDGE,"E40.2");Q1=makeQuery(id+"F11.opFillet","BLEND_EDGE",EDGE,{"blendedFrom":[makeQuery(id+"F10.boolean.opBoolean","SPLIT",EDGE,{"disambiguationData":[TD([makeQuery(id+"F7.opExtrude","SWEPT_FACE",FACE,{"disambiguationData":[OSD([subQ1])]}),makeQuery(id+"F7.opExtrude","CAP_FACE",FACE,{"disambiguationData":[OSD([subQ1,subQ0,subQ3,sQuery(id+"F6.wireOp",EDGE,"E40.3"),sQuery(id+"F6.wireOp",EDGE,"E40.4"),sQuery(id+"F6.wireOp",EDGE,"E40.5"),sQuery(id+"F6.wireOp",EDGE,"E40.6"),sQuery(id+"F6.wireOp",EDGE,"E40.7")])],"isStart":false}),makeQuery(id+"F7.opExtrude","SWEPT_FACE",FACE,{"disambiguationData":[OSD([subQ3])]}),makeQuery(id+"F10.opRevolve","SWEPT_FACE",FACE,{"disambiguationData":[OSD([subQ2])]})])],"derivedFrom":makeQuery(id+"F10.opRevolve","SWEPT_EDGE",EDGE,{"disambiguationData":[OSD([subQ2,sQuery(id+"F9.wireOp",EDGE,"E44")])]})}),makeQuery(id+"F7.opExtrude","SWEPT_FACE",FACE,{"disambiguationData":[OSD([subQ0])]})],"blendedInto":[makeQuery(id+"F7.opExtrude","SWEPT_FACE",FACE,{"disambiguationData":[OSD([subQ0])]})]});}
            var Q2;
            {var subQ0=sQuery(id+"F6.wireOp",EDGE,"E40.3");var subQ1=sQuery(id+"F6.wireOp",EDGE,"E40.4");var subQ2=sQuery(id+"F6.wireOp",EDGE,"E40.2");var subQ3=sQuery(id+"F9.wireOp",EDGE,"E43");Q2=makeQuery(id+"F11.opFillet","BLEND_EDGE",EDGE,{"blendedFrom":[makeQuery(id+"F10.boolean.opBoolean","SPLIT",EDGE,{"disambiguationData":[TD([makeQuery(id+"F7.opExtrude","CAP_FACE",FACE,{"disambiguationData":[OSD([sQuery(id+"F6.wireOp",EDGE,"E40.0"),sQuery(id+"F6.wireOp",EDGE,"E40.1"),subQ2,subQ0,subQ1,sQuery(id+"F6.wireOp",EDGE,"E40.5"),sQuery(id+"F6.wireOp",EDGE,"E40.6"),sQuery(id+"F6.wireOp",EDGE,"E40.7")])],"isStart":false}),makeQuery(id+"F7.opExtrude","SWEPT_FACE",FACE,{"disambiguationData":[OSD([subQ2])]}),makeQuery(id+"F7.opExtrude","SWEPT_FACE",FACE,{"disambiguationData":[OSD([subQ1])]}),makeQuery(id+"F10.opRevolve","SWEPT_FACE",FACE,{"disambiguationData":[OSD([subQ3])]})])],"derivedFrom":makeQuery(id+"F10.opRevolve","SWEPT_EDGE",EDGE,{"disambiguationData":[OSD([subQ3,sQuery(id+"F9.wireOp",EDGE,"E44")])]})}),makeQuery(id+"F7.opExtrude","SWEPT_FACE",FACE,{"disambiguationData":[OSD([subQ0])]})],"blendedInto":[makeQuery(id+"F7.opExtrude","SWEPT_FACE",FACE,{"disambiguationData":[OSD([subQ0])]})]});}
            var Q3;
            {var subQ0=sQuery(id+"F6.wireOp",EDGE,"E40.5");var subQ1=sQuery(id+"F6.wireOp",EDGE,"E40.6");var subQ2=sQuery(id+"F6.wireOp",EDGE,"E40.4");var subQ3=sQuery(id+"F9.wireOp",EDGE,"E43");Q3=makeQuery(id+"F11.opFillet","BLEND_EDGE",EDGE,{"blendedFrom":[makeQuery(id+"F10.boolean.opBoolean","SPLIT",EDGE,{"disambiguationData":[TD([makeQuery(id+"F7.opExtrude","CAP_FACE",FACE,{"disambiguationData":[OSD([sQuery(id+"F6.wireOp",EDGE,"E40.0"),sQuery(id+"F6.wireOp",EDGE,"E40.1"),sQuery(id+"F6.wireOp",EDGE,"E40.2"),sQuery(id+"F6.wireOp",EDGE,"E40.3"),subQ2,subQ0,subQ1,sQuery(id+"F6.wireOp",EDGE,"E40.7")])],"isStart":false}),makeQuery(id+"F7.opExtrude","SWEPT_FACE",FACE,{"disambiguationData":[OSD([subQ2])]}),makeQuery(id+"F7.opExtrude","SWEPT_FACE",FACE,{"disambiguationData":[OSD([subQ1])]}),makeQuery(id+"F10.opRevolve","SWEPT_FACE",FACE,{"disambiguationData":[OSD([subQ3])]})])],"derivedFrom":makeQuery(id+"F10.opRevolve","SWEPT_EDGE",EDGE,{"disambiguationData":[OSD([subQ3,sQuery(id+"F9.wireOp",EDGE,"E44")])]})}),makeQuery(id+"F7.opExtrude","SWEPT_FACE",FACE,{"disambiguationData":[OSD([subQ0])]})],"blendedInto":[makeQuery(id+"F7.opExtrude","SWEPT_FACE",FACE,{"disambiguationData":[OSD([subQ0])]})]});}
            fillet(context, id + "F12", {"entities" : qUnion([Q0, Q1, Q2, Q3]), "radius" : 2 * mm, "tangentPropagation" : true, "allowEdgeOverflow" : false});
        }
        {
            var Q0;
            Q0=makeQuery(id+"F1.opExtrude","CAP_FACE",FACE,{"disambiguationData":[OSD([sQuery(id+"F0.wireOp",EDGE,"E0.bottom"),sQuery(id+"F0.wireOp",EDGE,"E0.top"),sQuery(id+"F0.wireOp",EDGE,"E0.left"),sQuery(id+"F0.wireOp",EDGE,"E0.right")])],"isStart":false});
            var sketch = newSketch(context, id + "F13", { "sketchPlane" : qUnion([Q0])});
            skLineSegment(sketch, "E48.0", {"start": v(-15, -20) * mm, "end": v(15, -20) * mm});
            skArc(sketch, "E48.1", {"start": v(-15, -20) * mm, "mid": v(-22.07, -17.07) * mm, "end": v(-25, -10) * mm});
            skArc(sketch, "E48.2", {"start": v(25, -10) * mm, "mid": v(22.07, -17.07) * mm, "end": v(15, -20) * mm});
            skLineSegment(sketch, "E48.3", {"start": v(25, -10) * mm, "end": v(25, 10) * mm});
            skLineSegment(sketch, "E48.4", {"start": v(-25, -10) * mm, "end": v(-25, 10) * mm});
            skArc(sketch, "E48.5", {"start": v(-25, 10) * mm, "mid": v(-22.07, 17.07) * mm, "end": v(-15, 20) * mm});
            skLineSegment(sketch, "E48.6", {"start": v(-15, 20) * mm, "end": v(15, 20) * mm});
            skArc(sketch, "E48.7", {"start": v(15, 20) * mm, "mid": v(22.07, 17.07) * mm, "end": v(25, 10) * mm});
            skArc(sketch, "E49.0", {"start": v(-15, -21.6) * mm, "mid": v(-23.2, -18.2) * mm, "end": v(-26.6, -10) * mm});
            skLineSegment(sketch, "E49.1", {"start": v(-26.6, -10) * mm, "end": v(-26.6, 10) * mm});
            skLineSegment(sketch, "E49.2", {"start": v(-15, -21.6) * mm, "end": v(15, -21.6) * mm});
            skArc(sketch, "E49.3", {"start": v(-26.6, 10) * mm, "mid": v(-23.2, 18.2) * mm, "end": v(-15, 21.6) * mm});
            skArc(sketch, "E49.4", {"start": v(26.6, -10) * mm, "mid": v(23.2, -18.2) * mm, "end": v(15, -21.6) * mm});
            skLineSegment(sketch, "E49.5", {"start": v(26.6, -10) * mm, "end": v(26.6, 10) * mm});
            skArc(sketch, "E49.6", {"start": v(15, 21.6) * mm, "mid": v(23.2, 18.2) * mm, "end": v(26.6, 10) * mm});
            skLineSegment(sketch, "E49.7", {"start": v(-15, 21.6) * mm, "end": v(15, 21.6) * mm});
            skSolve(sketch);
        }
        {
            var Q0;
            Q0 = qSketchRegion(id + "F13", true);
            var Q1;
            Q1=makeQuery(id+"F3.opExtrude","CAP_FACE",FACE,{"disambiguationData":[OSD([sQuery(id+"F2.wireOp",EDGE,"E3"),sQuery(id+"F2.wireOp",EDGE,"E4"),sQuery(id+"F2.wireOp",EDGE,"E5"),sQuery(id+"F2.wireOp",EDGE,"E6"),sQuery(id+"F2.wireOp",EDGE,"E7"),sQuery(id+"F2.wireOp",EDGE,"E8"),sQuery(id+"F2.wireOp",EDGE,"E9"),sQuery(id+"F2.wireOp",EDGE,"E10"),sQuery(id+"F2.wireOp",EDGE,"E11"),sQuery(id+"F2.wireOp",EDGE,"E12"),sQuery(id+"F2.wireOp",EDGE,"E13"),sQuery(id+"F2.wireOp",EDGE,"E18"),sQuery(id+"F2.wireOp",EDGE,"E19"),sQuery(id+"F2.wireOp",EDGE,"E20"),sQuery(id+"F2.wireOp",EDGE,"E21"),sQuery(id+"F2.wireOp",EDGE,"E22"),sQuery(id+"F2.wireOp",EDGE,"E23"),sQuery(id+"F2.wireOp",EDGE,"E24"),sQuery(id+"F2.wireOp",EDGE,"E25"),sQuery(id+"F2.wireOp",EDGE,"E26"),sQuery(id+"F2.wireOp",EDGE,"E27"),sQuery(id+"F2.wireOp",EDGE,"E28"),sQuery(id+"F2.wireOp",EDGE,"E29"),sQuery(id+"F2.wireOp",EDGE,"E30")])],"isStart":false});
            extrude(context, id + "F14", {"entities" : qUnion([Q0]), "endBound" : BoundingType.UP_TO_SURFACE, "oppositeDirection" : true, "depth" : 25 * mm, "endBoundEntityFace" : qUnion([Q1]), "offsetDistance" : 25 * mm});
        }
        {
            var Q0;
            Q0=makeQuery(id+"F14.opExtrude","CAP_FACE",FACE,{"disambiguationData":[OSD([sQuery(id+"F13.wireOp",EDGE,"E48.0"),sQuery(id+"F13.wireOp",EDGE,"E48.1"),sQuery(id+"F13.wireOp",EDGE,"E48.2"),sQuery(id+"F13.wireOp",EDGE,"E48.3"),sQuery(id+"F13.wireOp",EDGE,"E48.4"),sQuery(id+"F13.wireOp",EDGE,"E48.5"),sQuery(id+"F13.wireOp",EDGE,"E48.6"),sQuery(id+"F13.wireOp",EDGE,"E48.7"),sQuery(id+"F13.wireOp",EDGE,"E49.0"),sQuery(id+"F13.wireOp",EDGE,"E49.1"),sQuery(id+"F13.wireOp",EDGE,"E49.2"),sQuery(id+"F13.wireOp",EDGE,"E49.3"),sQuery(id+"F13.wireOp",EDGE,"E49.4"),sQuery(id+"F13.wireOp",EDGE,"E49.5"),sQuery(id+"F13.wireOp",EDGE,"E49.6"),sQuery(id+"F13.wireOp",EDGE,"E49.7")])],"isStart":false});
            var sketch = newSketch(context, id + "F15", { "sketchPlane" : qUnion([Q0])});
            skArc(sketch, "E50.0", {"start": v(-15, 21.6) * mm, "mid": v(-23.2, 18.2) * mm, "end": v(-26.6, 10) * mm});
            skLineSegment(sketch, "E50.1", {"start": v(-15, 21.6) * mm, "end": v(15, 21.6) * mm});
            skArc(sketch, "E50.2", {"start": v(26.6, 10) * mm, "mid": v(23.2, 18.2) * mm, "end": v(15, 21.6) * mm});
            skLineSegment(sketch, "E50.3", {"start": v(26.6, 10) * mm, "end": v(26.6, -10) * mm});
            skArc(sketch, "E50.4", {"start": v(15, -21.6) * mm, "mid": v(23.2, -18.2) * mm, "end": v(26.6, -10) * mm});
            skLineSegment(sketch, "E50.5", {"start": v(-15, -21.6) * mm, "end": v(15, -21.6) * mm});
            skArc(sketch, "E50.6", {"start": v(-26.6, -10) * mm, "mid": v(-23.2, -18.2) * mm, "end": v(-15, -21.6) * mm});
            skLineSegment(sketch, "E50.7", {"start": v(-26.6, 10) * mm, "end": v(-26.6, -10) * mm});
            skSolve(sketch);
        }
        {
            var Q0;
            Q0 = qSketchRegion(id + "F15", true);
            extrude(context, id + "F16", {"entities" : qUnion([Q0]), "operationType" : NewBodyOperationType.ADD, "depth" : 1 * mm, "offsetDistance" : 25 * mm});
        }
        {
            var Q0;
            Q0=makeQuery(id+"F14.opExtrude","CAP_FACE",FACE,{"disambiguationData":[OSD([sQuery(id+"F13.wireOp",EDGE,"E48.0"),sQuery(id+"F13.wireOp",EDGE,"E48.1"),sQuery(id+"F13.wireOp",EDGE,"E48.2"),sQuery(id+"F13.wireOp",EDGE,"E48.3"),sQuery(id+"F13.wireOp",EDGE,"E48.4"),sQuery(id+"F13.wireOp",EDGE,"E48.5"),sQuery(id+"F13.wireOp",EDGE,"E48.6"),sQuery(id+"F13.wireOp",EDGE,"E48.7"),sQuery(id+"F13.wireOp",EDGE,"E49.0"),sQuery(id+"F13.wireOp",EDGE,"E49.1"),sQuery(id+"F13.wireOp",EDGE,"E49.2"),sQuery(id+"F13.wireOp",EDGE,"E49.3"),sQuery(id+"F13.wireOp",EDGE,"E49.4"),sQuery(id+"F13.wireOp",EDGE,"E49.5"),sQuery(id+"F13.wireOp",EDGE,"E49.6"),sQuery(id+"F13.wireOp",EDGE,"E49.7")])],"isStart":true});
            var sketch = newSketch(context, id + "F17", { "sketchPlane" : qUnion([Q0])});
            skLineSegment(sketch, "E51.0", {"start": v(25, -10) * mm, "end": v(25, 10) * mm});
            skLineSegment(sketch, "E51.1", {"start": v(26.6, -10) * mm, "end": v(26.6, 10) * mm});
            skLineSegment(sketch, "E51.2", {"start": v(-15, -20) * mm, "end": v(15, -20) * mm});
            skLineSegment(sketch, "E51.3", {"start": v(-15, -21.6) * mm, "end": v(15, -21.6) * mm});
            skLineSegment(sketch, "E51.4", {"start": v(-26.6, -10) * mm, "end": v(-26.6, 10) * mm});
            skLineSegment(sketch, "E51.5", {"start": v(-25, -10) * mm, "end": v(-25, 10) * mm});
            skLineSegment(sketch, "E51.6", {"start": v(-15, 21.6) * mm, "end": v(15, 21.6) * mm});
            skLineSegment(sketch, "E51.7", {"start": v(-15, 20) * mm, "end": v(15, 20) * mm});
            skLineSegment(sketch, "E52", {"start": v(26.6, -10) * mm, "end": v(25, -10) * mm});
            skLineSegment(sketch, "E53", {"start": v(26.6, 10) * mm, "end": v(25, 10) * mm});
            skLineSegment(sketch, "E54", {"start": v(15, 20) * mm, "end": v(15, 21.6) * mm});
            skLineSegment(sketch, "E55", {"start": v(-15, 21.6) * mm, "end": v(-15, 20) * mm});
            skLineSegment(sketch, "E56", {"start": v(-26.6, 10) * mm, "end": v(-25, 10) * mm});
            skLineSegment(sketch, "E57", {"start": v(-26.6, -10) * mm, "end": v(-25, -10) * mm});
            skLineSegment(sketch, "E58", {"start": v(-15, -20) * mm, "end": v(-15, -21.6) * mm});
            skLineSegment(sketch, "E59", {"start": v(15, -20) * mm, "end": v(15, -21.6) * mm});
            skSolve(sketch);
        }
        {
            var Q0;
            Q0 = qSketchRegion(id + "F17", true);
            extrude(context, id + "F18", {"entities" : qUnion([Q0]), "operationType" : NewBodyOperationType.REMOVE, "oppositeDirection" : true, "depth" : 4 * mm, "offsetDistance" : 25 * mm});
        }
        {
            var Q0;
            Q0=makeQuery(id+"F18.boolean.opBoolean","COPY",EDGE,{"derivedFrom":makeQuery(id+"F18.opExtrude","CAP_EDGE",EDGE,{"disambiguationData":[OSD([sQuery(id+"F17.wireOp",EDGE,"E58")])],"isStart":false})});
            var Q1;
            Q1=makeQuery(id+"F18.boolean.opBoolean","COPY",EDGE,{"derivedFrom":makeQuery(id+"F18.opExtrude","CAP_EDGE",EDGE,{"disambiguationData":[OSD([sQuery(id+"F17.wireOp",EDGE,"E58")])],"isStart":true})});
            var Q2;
            Q2=makeQuery(id+"F18.boolean.opBoolean","COPY",EDGE,{"derivedFrom":makeQuery(id+"F18.opExtrude","CAP_EDGE",EDGE,{"disambiguationData":[OSD([sQuery(id+"F17.wireOp",EDGE,"E59")])],"isStart":true})});
            var Q3;
            Q3=makeQuery(id+"F18.boolean.opBoolean","COPY",EDGE,{"derivedFrom":makeQuery(id+"F18.opExtrude","CAP_EDGE",EDGE,{"disambiguationData":[OSD([sQuery(id+"F17.wireOp",EDGE,"E52")])],"isStart":true})});
            var Q4;
            Q4=makeQuery(id+"F18.boolean.opBoolean","COPY",EDGE,{"derivedFrom":makeQuery(id+"F18.opExtrude","CAP_EDGE",EDGE,{"disambiguationData":[OSD([sQuery(id+"F17.wireOp",EDGE,"E53")])],"isStart":true})});
            var Q5;
            Q5=makeQuery(id+"F18.boolean.opBoolean","COPY",EDGE,{"derivedFrom":makeQuery(id+"F18.opExtrude","CAP_EDGE",EDGE,{"disambiguationData":[OSD([sQuery(id+"F17.wireOp",EDGE,"E54")])],"isStart":true})});
            var Q6;
            Q6=makeQuery(id+"F18.boolean.opBoolean","COPY",EDGE,{"derivedFrom":makeQuery(id+"F18.opExtrude","CAP_EDGE",EDGE,{"disambiguationData":[OSD([sQuery(id+"F17.wireOp",EDGE,"E56")])],"isStart":true})});
            var Q7;
            Q7=makeQuery(id+"F18.boolean.opBoolean","COPY",EDGE,{"derivedFrom":makeQuery(id+"F18.opExtrude","CAP_EDGE",EDGE,{"disambiguationData":[OSD([sQuery(id+"F17.wireOp",EDGE,"E57")])],"isStart":true})});
            var Q8;
            Q8=makeQuery(id+"F18.boolean.opBoolean","COPY",EDGE,{"derivedFrom":makeQuery(id+"F18.opExtrude","CAP_EDGE",EDGE,{"disambiguationData":[OSD([sQuery(id+"F17.wireOp",EDGE,"E55")])],"isStart":true})});
            var Q9;
            Q9=makeQuery(id+"F18.boolean.opBoolean","COPY",EDGE,{"derivedFrom":makeQuery(id+"F18.opExtrude","CAP_EDGE",EDGE,{"disambiguationData":[OSD([sQuery(id+"F17.wireOp",EDGE,"E59")])],"isStart":false})});
            var Q10;
            Q10=makeQuery(id+"F18.boolean.opBoolean","COPY",EDGE,{"derivedFrom":makeQuery(id+"F18.opExtrude","CAP_EDGE",EDGE,{"disambiguationData":[OSD([sQuery(id+"F17.wireOp",EDGE,"E56")])],"isStart":false})});
            var Q11;
            Q11=makeQuery(id+"F18.boolean.opBoolean","COPY",EDGE,{"derivedFrom":makeQuery(id+"F18.opExtrude","CAP_EDGE",EDGE,{"disambiguationData":[OSD([sQuery(id+"F17.wireOp",EDGE,"E52")])],"isStart":false})});
            var Q12;
            Q12=makeQuery(id+"F18.boolean.opBoolean","COPY",EDGE,{"derivedFrom":makeQuery(id+"F18.opExtrude","CAP_EDGE",EDGE,{"disambiguationData":[OSD([sQuery(id+"F17.wireOp",EDGE,"E55")])],"isStart":false})});
            var Q13;
            Q13=makeQuery(id+"F18.boolean.opBoolean","COPY",EDGE,{"derivedFrom":makeQuery(id+"F18.opExtrude","CAP_EDGE",EDGE,{"disambiguationData":[OSD([sQuery(id+"F17.wireOp",EDGE,"E54")])],"isStart":false})});
            var Q14;
            Q14=makeQuery(id+"F18.boolean.opBoolean","COPY",EDGE,{"derivedFrom":makeQuery(id+"F18.opExtrude","CAP_EDGE",EDGE,{"disambiguationData":[OSD([sQuery(id+"F17.wireOp",EDGE,"E57")])],"isStart":false})});
            var Q15;
            Q15=makeQuery(id+"F18.boolean.opBoolean","COPY",EDGE,{"derivedFrom":makeQuery(id+"F18.opExtrude","CAP_EDGE",EDGE,{"disambiguationData":[OSD([sQuery(id+"F17.wireOp",EDGE,"E53")])],"isStart":false})});
            fillet(context, id + "F19", {"entities" : qUnion([Q0, Q1, Q2, Q3, Q4, Q5, Q6, Q7, Q8, Q9, Q10, Q11, Q12, Q13, Q14, Q15]), "radius" : 2 * mm, "tangentPropagation" : true, "allowEdgeOverflow" : false});
        }
    });
